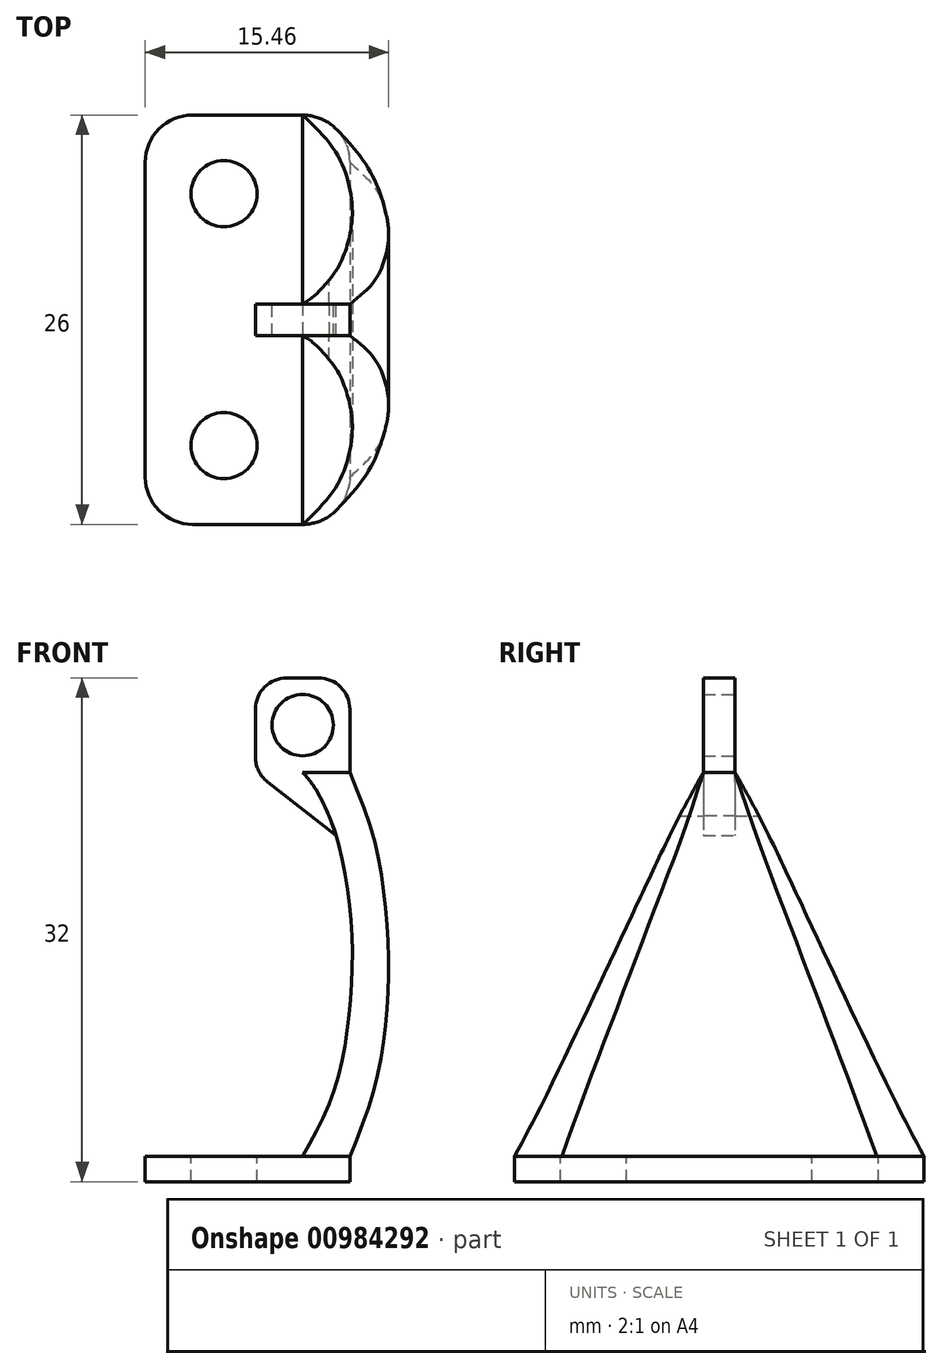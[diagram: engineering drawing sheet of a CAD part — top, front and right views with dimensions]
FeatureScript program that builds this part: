
annotation { "Feature Type Name" : "Feature", "Feature Type Description" : "" }
export const myFeature = defineFeature(function(context is Context, id is Id, definition is map)
    precondition{}
    {
        {
            var Q0;
            Q0=qCreatedBy(makeId("Top.planeOp"),FACE);
            var sketch = newSketch(context, id + "F0", { "sketchPlane" : qUnion([Q0])});
            skLineSegment(sketch, "E0.bottom", {"start": v(-2, 13) * mm, "end": v(5, 13) * mm});
            skLineSegment(sketch, "E0.top", {"start": v(-2, -13) * mm, "end": v(5, -13) * mm});
            skLineSegment(sketch, "E0.left", {"start": v(-5, 10) * mm, "end": v(-5, -10) * mm});
            skLineSegment(sketch, "E0.right", {"start": v(8, 10) * mm, "end": v(8, -10) * mm});
            skPoint(sketch, "E0.middle", {"position": v(0, -2) * mm});
            skCircle(sketch, "E1", {"center": v(0, 8) * mm, "radius": 2.1 * mm});
            skCircle(sketch, "E2", {"center": v(0, -8) * mm, "radius": 2.1 * mm});
            skLineSegment(sketch, "E3", {"start": v(5, 13) * mm, "end": v(5, -13) * mm});
            skPoint(sketch, "E4.visualSharp", {"position": v(-5, 13) * mm});
            skArc(sketch, "E4.filletArc", {"start": v(-2, 13) * mm, "mid": v(-4.12, 12.12) * mm, "end": v(-5, 10) * mm});
            skPoint(sketch, "E5.visualSharp", {"position": v(8, 13) * mm});
            skArc(sketch, "E5.filletArc", {"start": v(8, 10) * mm, "mid": v(7.12, 12.12) * mm, "end": v(5, 13) * mm});
            skPoint(sketch, "E6.visualSharp", {"position": v(8, -13) * mm});
            skArc(sketch, "E6.filletArc", {"start": v(5, -13) * mm, "mid": v(7.12, -12.12) * mm, "end": v(8, -10) * mm});
            skPoint(sketch, "E7.visualSharp", {"position": v(-5, -13) * mm});
            skArc(sketch, "E7.filletArc", {"start": v(-5, -10) * mm, "mid": v(-4.12, -12.12) * mm, "end": v(-2, -13) * mm});
            skPoint(sketch, "E8.middle", {"position": v(5, 0) * mm});
            skSolve(sketch);
        }
        {
            var Q0;
            {var subQ4=sQuery(id+"F0.wireOp",EDGE,"E0.bottom");Q0=makeQuery(id+"F0.imprint","IMPRINT",FACE,{"disambiguationData":[TD([[makeQuery(id+"F0.imprint","IMPRINT",EDGE,{"derivedFrom":subQ4}),-1.0]])]});}
            var Q1;
            {var subQ5=sQuery(id+"F0.wireOp",EDGE,"E8.left");Q1=makeQuery(id+"F0.imprint","IMPRINT",FACE,{"disambiguationData":[TD([[makeQuery(id+"F0.imprint","IMPRINT",EDGE,{"derivedFrom":subQ5}),1.0]])]});}
            var Q2;
            {var subQ5=sQuery(id+"F0.wireOp",EDGE,"E8.right");Q2=makeQuery(id+"F0.imprint","IMPRINT",FACE,{"disambiguationData":[TD([[makeQuery(id+"F0.imprint","IMPRINT",EDGE,{"derivedFrom":subQ5}),-1.0]])]});}
            var Q3;
            Q3=makeQuery(id+"F0.imprint","IMPRINT",FACE,{"disambiguationData":[TD([[makeQuery(id+"F0.imprint","IMPRINT",EDGE,{"derivedFrom":sQuery(id+"F0.wireOp",EDGE,"E0.right")}),-1.0]])]});
            var Q4;
            {var subQ0=sQuery(id+"F0.wireOp",EDGE,"xKevLc2L-wJd7-obCB-2kap-YXjd5JsPCSwG");Q4=makeQuery(id+"F0.imprint","IMPRINT",FACE,{"disambiguationData":[TD([[makeQuery(id+"F0.imprint","IMPRINT",EDGE,{"derivedFrom":subQ0}),-1.0]])]});}
            extrude(context, id + "F1", {"entities" : qUnion([Q0, Q1, Q2, Q3, Q4]), "oppositeDirection" : true, "depth" : 1.6 * mm, "offsetDistance" : 25 * mm});
        }
        {
            var Q0;
            Q0=qCreatedBy(makeId("Top.planeOp"),FACE);
            var sketch = newSketch(context, id + "F2", { "sketchPlane" : qUnion([Q0])});
            skLineSegment(sketch, "E9.bottom", {"start": v(5, 1) * mm, "end": v(8, 1) * mm});
            skLineSegment(sketch, "E9.top", {"start": v(5, -1) * mm, "end": v(8, -1) * mm});
            skLineSegment(sketch, "E9.left", {"start": v(5, 1) * mm, "end": v(5, -1) * mm});
            skLineSegment(sketch, "E9.right", {"start": v(8, 1) * mm, "end": v(8, -1) * mm});
            skLineSegment(sketch, "E10.bottom", {"start": v(5, 1) * mm, "end": v(2, 1) * mm});
            skLineSegment(sketch, "E10.top", {"start": v(5, -1) * mm, "end": v(2, -1) * mm});
            skLineSegment(sketch, "E10.right", {"start": v(2, 1) * mm, "end": v(2, -1) * mm});
            skSolve(sketch);
        }
        {
            var Q0;
            Q0=makeQuery(id+"F2.imprint","IMPRINT",FACE,{"disambiguationData":[TD([[makeQuery(id+"F2.imprint","IMPRINT",EDGE,{"derivedFrom":sQuery(id+"F2.wireOp",EDGE,"E9.bottom")}),-1.0]])]});
            extrude(context, id + "F3", {"entities" : qUnion([Q0]), "depth" : 30.4 * mm, "offsetDistance" : 25 * mm, "hasSecondDirection" : true, "secondDirectionOppositeDirection" : false, "secondDirectionDepth" : 24.4 * mm});
        }
        {
            var Q0;
            Q0=qCreatedBy(makeId("Front.planeOp"),FACE);
            var sketch = newSketch(context, id + "F4", { "sketchPlane" : qUnion([Q0])});
            skCircle(sketch, "E11", {"center": v(5, 27.4) * mm, "radius": 1.95 * mm});
            skLineSegment(sketch, "E12", {"start": v(5, 24.4) * mm, "end": v(2, 24.4) * mm});
            skFitSpline(sketch, "E13", {"points": [v(5, 24.4) * mm, v(5, 0) * mm], "startDerivative": vector(11.76, -12.23) * mm, "endDerivative": vector(-13.46, -19.02) * mm});
            skLineSegment(sketch, "E14", {"start": v(2, 24.4) * mm, "end": v(7.1, 20.38) * mm});
            skSolve(sketch);
        }
        {
            var Q0;
            Q0=sQuery(id+"F4.wireOp",EDGE,"E13");
            var Q2;
            Q2=makeQuery(id+"F0.imprint","IMPRINT",FACE,{"disambiguationData":[TD([[makeQuery(id+"F0.imprint","IMPRINT",EDGE,{"derivedFrom":sQuery(id+"F0.wireOp",EDGE,"E0.right")}),-1.0]])]});
            var Q3;
            Q3=makeQuery(id+"F3.opExtrude","CAP_FACE",FACE,{"disambiguationData":[OSD([sQuery(id+"F2.wireOp",EDGE,"E9.bottom"),sQuery(id+"F2.wireOp",EDGE,"E9.top"),sQuery(id+"F2.wireOp",EDGE,"E9.right"),sQuery(id+"F2.wireOp",EDGE,"E9.left")])],"isStart":true});
            loft(context, id + "F5", {"operationType" : NewBodyOperationType.ADD, "addSections" : true, "spine" : qUnion([Q0]), "sectionCount" : 5, "sheetProfilesArray" : [{ "sheetProfileEntities" : qUnion([Q2]) }, { "sheetProfileEntities" : qUnion([Q3]) }]});
        }
        {
            var Q0;
            Q0=makeQuery(id+"F2.imprint","IMPRINT",FACE,{"disambiguationData":[TD([[makeQuery(id+"F2.imprint","IMPRINT",EDGE,{"derivedFrom":sQuery(id+"F2.wireOp",EDGE,"E10.bottom")}),1.0]])]});
            extrude(context, id + "F6", {"entities" : qUnion([Q0]), "operationType" : NewBodyOperationType.ADD, "depth" : 30.4 * mm, "offsetDistance" : 25 * mm, "hasSecondDirection" : true, "secondDirectionOppositeDirection" : false, "secondDirectionDepth" : 24.4 * mm});
        }
        {
            var Q0;
            Q0 = qSketchRegion(id + "F4", true);
            extrude(context, id + "F7", {"entities" : qUnion([Q0]), "operationType" : NewBodyOperationType.REMOVE, "endBound" : BoundingType.THROUGH_ALL, "depth" : 25 * mm, "offsetDistance" : 25 * mm, "hasSecondDirection" : true, "secondDirectionBound" : SecondDirectionBoundingType.THROUGH_ALL, "secondDirectionOppositeDirection" : true, "secondDirectionDepth" : 25 * mm});
        }
        {
            var Q0;
            Q0=makeQuery(id+"F4.imprint","IMPRINT",FACE,{"disambiguationData":[TD([[makeQuery(id+"F4.imprint","IMPRINT",EDGE,{"derivedFrom":sQuery(id+"F4.wireOp",EDGE,"yFZFN4LA-7g9S-6GBV-4qa9-JL9CP4cKiioE")}),1.0]])]});
            var Q1;
            {var subQ0=sQuery(id+"F4.wireOp",EDGE,"E12");Q1=makeQuery(id+"F4.imprint","IMPRINT",FACE,{"disambiguationData":[TD([[makeQuery(id+"F4.imprint","IMPRINT",EDGE,{"derivedFrom":subQ0}),1.0]])]});}
            extrude(context, id + "F8", {"entities" : qUnion([Q0, Q1]), "operationType" : NewBodyOperationType.ADD, "depth" : 1 * mm, "offsetDistance" : 25 * mm, "hasSecondDirection" : true, "secondDirectionOppositeDirection" : true, "secondDirectionDepth" : 1 * mm});
        }
        {
            var Q0;
            Q0=makeQuery(id+"F3.opExtrude","CAP_EDGE",EDGE,{"disambiguationData":[OSD([sQuery(id+"F2.wireOp",EDGE,"E9.right")])],"isStart":false});
            var Q1;
            Q1=makeQuery(id+"F6.opExtrude","CAP_EDGE",EDGE,{"disambiguationData":[OSD([sQuery(id+"F2.wireOp",EDGE,"E10.right")])],"isStart":false});
            var Q2;
            Q2=makeQuery(id+"F8.boolean.opBoolean","MERGE",EDGE,{"derivedFrom":[makeQuery(id+"F6.opExtrude","CAP_EDGE",EDGE,{"disambiguationData":[OSD([sQuery(id+"F2.wireOp",EDGE,"E10.right")])],"isStart":true}),makeQuery(id+"F8.opExtrude","SWEPT_EDGE",EDGE,{"disambiguationData":[OSD([sQuery(id+"F4.wireOp",EDGE,"yFZFN4LA-7g9S-6GBV-4qa9-JL9CP4cKiioE"),sQuery(id+"F4.wireOp",EDGE,"E12")])]})]});
            fillet(context, id + "F9", {"entities" : qUnion([Q0, Q1, Q2]), "tangentPropagation" : true, "radius" : 2 * mm, "defaultsChanged" : false, "vertexSettings" : [], "allowEdgeOverflow" : false});
        }
    });
